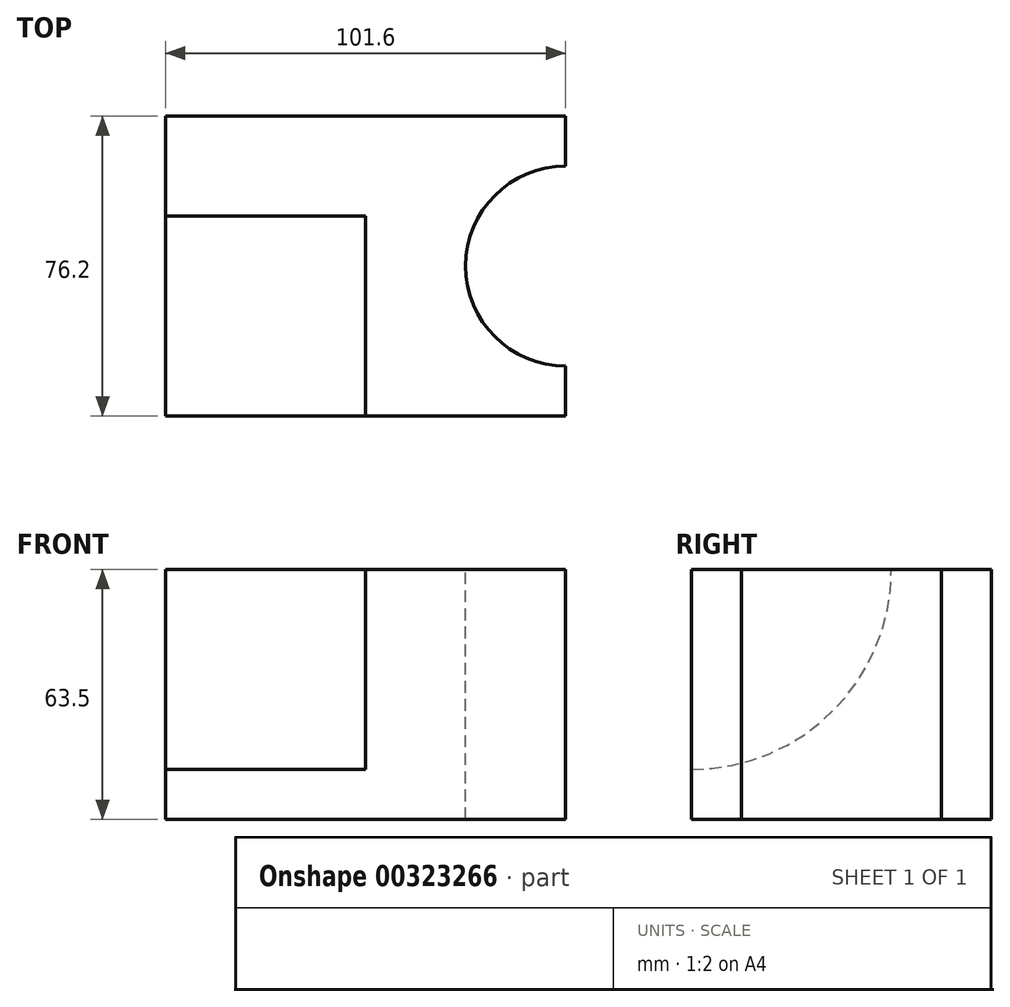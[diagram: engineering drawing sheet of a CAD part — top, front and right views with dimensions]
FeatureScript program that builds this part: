
annotation { "Feature Type Name" : "Feature", "Feature Type Description" : "" }
export const myFeature = defineFeature(function(context is Context, id is Id, definition is map)
    precondition{}
    {
        {
            var Q0;
            Q0=qCreatedBy(makeId("Front.planeOp"),FACE);
            var sketch = newSketch(context, id + "F0", { "sketchPlane" : qUnion([Q0])});
            skLineSegment(sketch, "E0", {"start": v(-45.77, 3.6) * mm, "end": v(-45.77, -59.9) * mm});
            skLineSegment(sketch, "E1", {"start": v(-45.77, -59.9) * mm, "end": v(55.83, -59.9) * mm});
            skLineSegment(sketch, "E2", {"start": v(55.83, -59.9) * mm, "end": v(55.83, 3.6) * mm});
            skLineSegment(sketch, "E3", {"start": v(55.83, 3.6) * mm, "end": v(-45.77, 3.6) * mm});
            skSolve(sketch);
        }
        {
            var Q0;
            Q0=makeQuery(id+"F0.imprint","IMPRINT",FACE,{"disambiguationData":[TD([[makeQuery(id+"F0.imprint","IMPRINT",EDGE,{"derivedFrom":sQuery(id+"F0.wireOp",EDGE,"E0")}),1.0]])]});
            extrude(context, id + "F1", {"entities" : qUnion([Q0]), "oppositeDirection" : true, "depth" : 76.2 * mm});
        }
        {
            var Q0;
            Q0=makeQuery(id+"F1.opExtrude","SWEPT_FACE",FACE,{"disambiguationData":[OSD([sQuery(id+"F0.wireOp",EDGE,"E3")])]});
            var sketch = newSketch(context, id + "F2", { "sketchPlane" : qUnion([Q0])});
            skCircle(sketch, "E4", {"center": v(55.83, 38.1) * mm, "radius": 25.4 * mm});
            skSolve(sketch);
        }
        {
            var Q0;
            {var subQ0=sQuery(id+"F2.wireOp",EDGE,"E4");var subQ1=makeQuery(id+"F1.opExtrude","SWEPT_EDGE",EDGE,{"disambiguationData":[OSD([sQuery(id+"F0.wireOp",EDGE,"E2"),sQuery(id+"F0.wireOp",EDGE,"E3")])]});var subQ2=makeQuery(id+"F2.imprint","INTERSECT",VERTEX,{"disambiguationData":[OD(0.0)],"derivedFrom":[subQ1,subQ0]});Q0=makeQuery(id+"F2.imprint","IMPRINT",FACE,{"disambiguationData":[TD([[makeQuery(id+"F2.imprint","IMPRINT",EDGE,{"disambiguationData":[TD([[subQ2,1.0]])],"derivedFrom":subQ0}),1.0]])]});}
            extrude(context, id + "F3", {"entities" : qUnion([Q0]), "operationType" : NewBodyOperationType.REMOVE, "oppositeDirection" : true, "depth" : 63.5 * mm});
        }
        {
            var Q0;
            Q0=makeQuery(id+"F1.opExtrude","SWEPT_FACE",FACE,{"disambiguationData":[OSD([sQuery(id+"F0.wireOp",EDGE,"E0")])]});
            var sketch = newSketch(context, id + "F4", { "sketchPlane" : qUnion([Q0])});
            skCircle(sketch, "E5", {"center": v(0, 3.6) * mm, "radius": 50.8 * mm});
            skSolve(sketch);
        }
        {
            var Q0;
            {var subQ0=sQuery(id+"F4.wireOp",EDGE,"E5");var subQ1=sQuery(id+"F0.wireOp",EDGE,"E0");var subQ4=makeQuery(id+"F1.opExtrude","CAP_EDGE",EDGE,{"disambiguationData":[OSD([subQ1])],"isStart":true});var subQ5=makeQuery(id+"F4.imprint","INTERSECT",VERTEX,{"derivedFrom":[subQ4,subQ0]});Q0=makeQuery(id+"F4.imprint","IMPRINT",FACE,{"disambiguationData":[TD([[makeQuery(id+"F4.imprint","IMPRINT",EDGE,{"disambiguationData":[TD([[subQ5,1.0]])],"derivedFrom":subQ0}),1.0]])]});}
            extrude(context, id + "F5", {"entities" : qUnion([Q0]), "operationType" : NewBodyOperationType.REMOVE, "oppositeDirection" : true, "depth" : 50.8 * mm});
        }
    });
